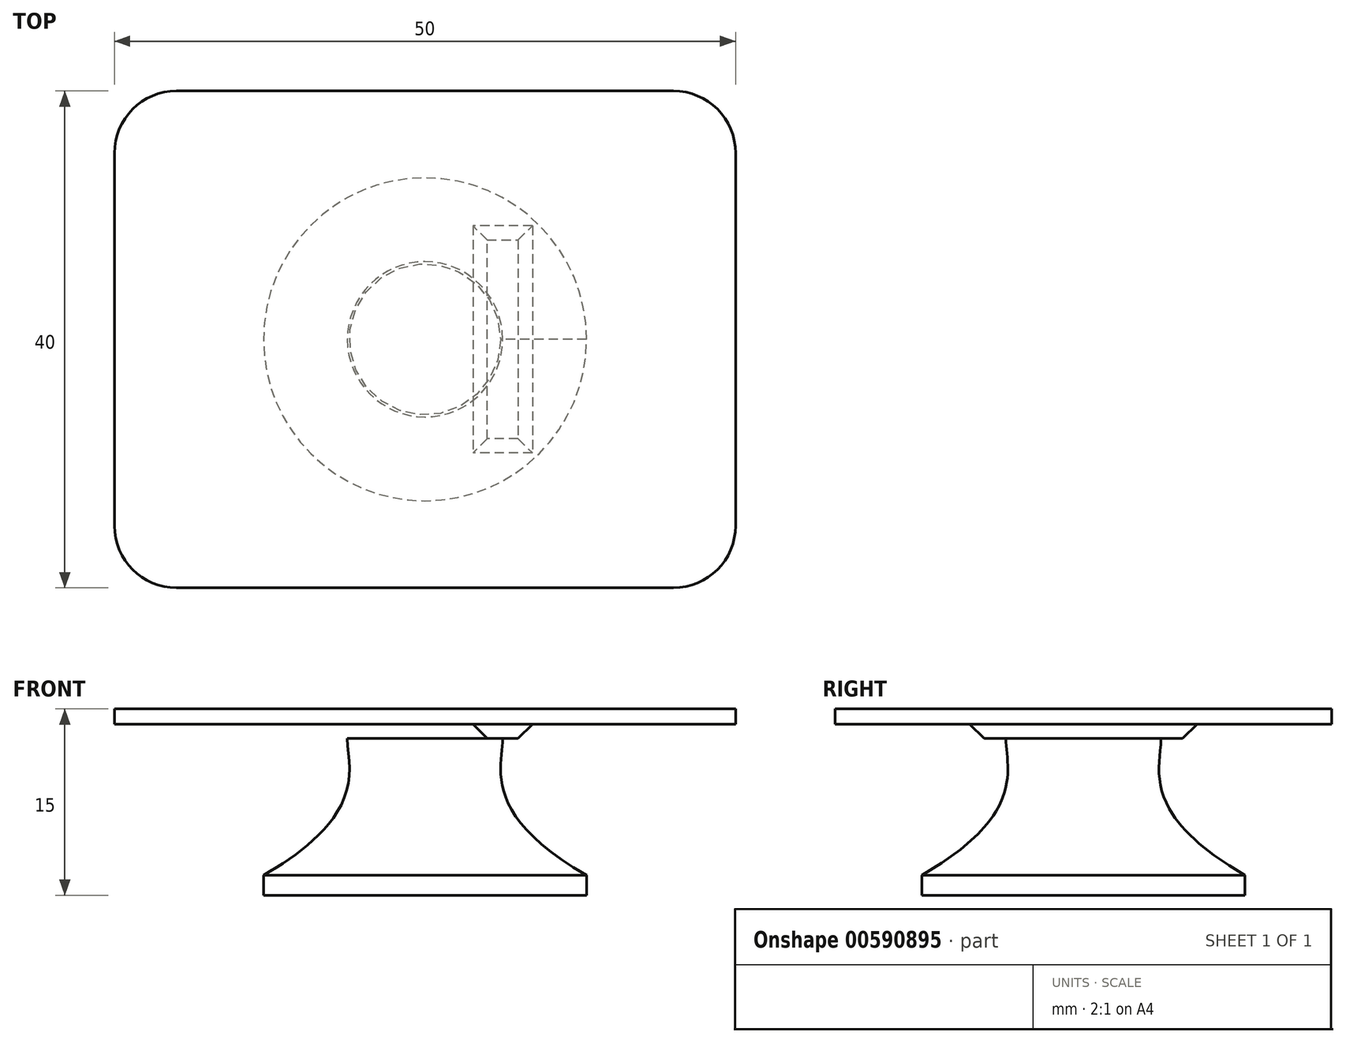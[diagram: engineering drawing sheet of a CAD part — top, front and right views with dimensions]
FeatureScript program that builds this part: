
annotation { "Feature Type Name" : "Feature", "Feature Type Description" : "" }
export const myFeature = defineFeature(function(context is Context, id is Id, definition is map)
    precondition{}
    {
        {
            var Q0;
            Q0=qCreatedBy(makeId("Front.planeOp"),FACE);
            var sketch = newSketch(context, id + "F0", { "sketchPlane" : qUnion([Q0])});
            skLineSegment(sketch, "E0.bottom", {"start": v(0, 15) * mm, "end": v(-25, 15) * mm});
            skLineSegment(sketch, "E0.top", {"start": v(0, 13.77) * mm, "end": v(-25, 13.77) * mm});
            skLineSegment(sketch, "E0.left", {"start": v(0, 15) * mm, "end": v(0, 13.77) * mm});
            skLineSegment(sketch, "E0.right", {"start": v(-25, 15) * mm, "end": v(-25, 13.77) * mm});
            skLineSegment(sketch, "E1.bottom", {"start": v(-12.5, 13.77) * mm, "end": v(0, 13.77) * mm});
            skLineSegment(sketch, "E1.top", {"start": v(-12.5, 12.62) * mm, "end": v(0, 12.62) * mm});
            skLineSegment(sketch, "E1.left", {"start": v(-12.5, 13.77) * mm, "end": v(-12.5, 12.62) * mm});
            skLineSegment(sketch, "E1.right", {"start": v(0, 13.77) * mm, "end": v(0, 12.62) * mm});
            skLineSegment(sketch, "E2.bottom", {"start": v(-13, 1.62) * mm, "end": v(0, 1.62) * mm});
            skLineSegment(sketch, "E2.top", {"start": v(-13, 0) * mm, "end": v(0, 0) * mm});
            skLineSegment(sketch, "E2.left", {"start": v(-13, 1.62) * mm, "end": v(-13, 0) * mm});
            skLineSegment(sketch, "E2.right", {"start": v(0, 1.62) * mm, "end": v(0, 0) * mm});
            skFitSpline(sketch, "E3", {"points": [v(-13, 1.62) * mm, v(-6.25, 12.62) * mm], "startDerivative": vector(25.82, 14.76) * mm, "endDerivative": vector(0.02, 6.66) * mm});
            skLineSegment(sketch, "E4", {"start": v(0, 15) * mm, "end": v(0, 0) * mm});
            skLineSegment(sketch, "E5.MirrorCS", {"start": v(13, 1.62) * mm, "end": v(13, 0) * mm});
            skLineSegment(sketch, "E6.MirrorCS", {"start": v(25, 15) * mm, "end": v(25, 13.77) * mm});
            skLineSegment(sketch, "E7.MirrorCS", {"start": v(12.5, 13.77) * mm, "end": v(12.5, 12.62) * mm});
            skFitSpline(sketch, "E8.MirrorCS", {"points": [v(13, 1.62) * mm, v(6.25, 12.62) * mm], "startDerivative": vector(-25.82, 14.76) * mm, "endDerivative": vector(-0.02, 6.66) * mm});
            skLineSegment(sketch, "E9.MirrorCS", {"start": v(13, 1.62) * mm, "end": v(0, 1.62) * mm});
            skLineSegment(sketch, "E10.MirrorCS", {"start": v(13, 0) * mm, "end": v(0, 0) * mm});
            skLineSegment(sketch, "E11.MirrorCS", {"start": v(0, 15) * mm, "end": v(25, 15) * mm});
            skLineSegment(sketch, "E12.MirrorCS", {"start": v(0, 13.77) * mm, "end": v(25, 13.77) * mm});
            skLineSegment(sketch, "E13.MirrorCS", {"start": v(12.5, 12.62) * mm, "end": v(0, 12.62) * mm});
            skLineSegment(sketch, "E14.MirrorCS", {"start": v(12.5, 13.77) * mm, "end": v(0, 13.77) * mm});
            skSolve(sketch);
        }
        {
            var Q0;
            Q0=makeQuery(id+"F0.imprint","IMPRINT",FACE,{"disambiguationData":[TD([[makeQuery(id+"F0.imprint","IMPRINT",EDGE,{"derivedFrom":sQuery(id+"F0.wireOp",EDGE,"E0.bottom")}),1.0]])]});
            var Q1;
            Q1=makeQuery(id+"F0.imprint","IMPRINT",FACE,{"disambiguationData":[TD([[makeQuery(id+"F0.imprint","IMPRINT",EDGE,{"derivedFrom":sQuery(id+"F0.wireOp",EDGE,"E0.left")}),1.0]])]});
            extrude(context, id + "F1", {"entities" : qUnion([Q0, Q1]), "endBound" : BoundingType.SYMMETRIC, "depth" : 40 * mm, "offsetDistance" : 25 * mm});
        }
        {
            var Q0;
            Q0=makeQuery(id+"F0.imprint","IMPRINT",FACE,{"disambiguationData":[TD([[makeQuery(id+"F0.imprint","IMPRINT",EDGE,{"derivedFrom":sQuery(id+"F0.wireOp",EDGE,"E1.bottom")}),-1.0]])]});
            var Q1;
            {var subQ3=sQuery(id+"F0.wireOp",EDGE,"E7.MirrorCS");Q1=makeQuery(id+"F0.imprint","IMPRINT",FACE,{"disambiguationData":[TD([[makeQuery(id+"F0.imprint","IMPRINT",EDGE,{"derivedFrom":subQ3}),-1.0]])]});}
            var Q2;
            Q2=makeQuery(id+"F0.imprint","IMPRINT",FACE,{"disambiguationData":[TD([[makeQuery(id+"F0.imprint","IMPRINT",EDGE,{"derivedFrom":sQuery(id+"F0.wireOp",EDGE,"E2.bottom")}),-1.0]])]});
            var Q3;
            Q3=makeQuery(id+"F0.imprint","IMPRINT",FACE,{"disambiguationData":[TD([[makeQuery(id+"F0.imprint","IMPRINT",EDGE,{"derivedFrom":sQuery(id+"F0.wireOp",EDGE,"E5.MirrorCS")}),-1.0]])]});
            extrude(context, id + "F2", {"entities" : qUnion([Q0, Q1, Q2, Q3]), "operationType" : NewBodyOperationType.ADD, "endBound" : BoundingType.SYMMETRIC, "depth" : 26 * mm, "offsetDistance" : 25 * mm});
        }
        {
            var Q0;
            Q0=makeQuery(id+"F0.imprint","IMPRINT",FACE,{"disambiguationData":[TD([[makeQuery(id+"F0.imprint","IMPRINT",EDGE,{"derivedFrom":sQuery(id+"F0.wireOp",EDGE,"E2.bottom")}),1.0]])]});
            var Q1;
            Q1=sQuery(id+"F0.wireOp",EDGE,"E4");
            revolve(context, id + "F3", {"entities" : qUnion([Q0]), "axis" : qUnion([Q1]), "revolveType" : RevolveType.FULL});
        }
        {
            var Q0;
            Q0=makeQuery(id+"F2.opExtrude","CAP_EDGE",EDGE,{"disambiguationData":[OSD([sQuery(id+"F0.wireOp",EDGE,"E1.top"),sQuery(id+"F0.wireOp",EDGE,"E13.MirrorCS")])],"isStart":true});
            var Q1;
            Q1=makeQuery(id+"F2.opExtrude","SWEPT_EDGE",EDGE,{"disambiguationData":[OSD([sQuery(id+"F0.wireOp",EDGE,"E1.top"),sQuery(id+"F0.wireOp",EDGE,"E1.left")])]});
            var Q2;
            Q2=makeQuery(id+"F2.opExtrude","SWEPT_EDGE",EDGE,{"disambiguationData":[OSD([sQuery(id+"F0.wireOp",EDGE,"E7.MirrorCS"),sQuery(id+"F0.wireOp",EDGE,"E13.MirrorCS")])]});
            var Q3;
            Q3=makeQuery(id+"F2.opExtrude","CAP_EDGE",EDGE,{"disambiguationData":[OSD([sQuery(id+"F0.wireOp",EDGE,"E1.top"),sQuery(id+"F0.wireOp",EDGE,"E13.MirrorCS")])],"isStart":false});
            chamfer(context, id + "F4", {"entities" : qUnion([Q0, Q1, Q2, Q3]), "width" : 5 * mm, "tangentPropagation" : true});
        }
        {
            var Q0;
            Q0=makeQuery(id+"F2.opExtrude","CAP_EDGE",EDGE,{"disambiguationData":[OSD([sQuery(id+"F0.wireOp",EDGE,"E2.left")])],"isStart":true});
            var Q1;
            Q1=makeQuery(id+"F2.opExtrude","CAP_EDGE",EDGE,{"disambiguationData":[OSD([sQuery(id+"F0.wireOp",EDGE,"E2.left")])],"isStart":false});
            var Q2;
            Q2=makeQuery(id+"F2.opExtrude","CAP_EDGE",EDGE,{"disambiguationData":[OSD([sQuery(id+"F0.wireOp",EDGE,"E5.MirrorCS")])],"isStart":false});
            var Q3;
            Q3=makeQuery(id+"F2.opExtrude","CAP_EDGE",EDGE,{"disambiguationData":[OSD([sQuery(id+"F0.wireOp",EDGE,"E5.MirrorCS")])],"isStart":true});
            fillet(context, id + "F5", {"entities" : qUnion([Q0, Q1, Q2, Q3]), "radius" : 5 * mm, "tangentPropagation" : true, "allowEdgeOverflow" : false});
        }
        {
            var Q0;
            Q0=makeQuery(id+"F1.opExtrude","CAP_EDGE",EDGE,{"disambiguationData":[OSD([sQuery(id+"F0.wireOp",EDGE,"E0.right")])],"isStart":false});
            var Q1;
            Q1=makeQuery(id+"F1.opExtrude","CAP_EDGE",EDGE,{"disambiguationData":[OSD([sQuery(id+"F0.wireOp",EDGE,"E0.right")])],"isStart":true});
            var Q2;
            Q2=makeQuery(id+"F1.opExtrude","CAP_EDGE",EDGE,{"disambiguationData":[OSD([sQuery(id+"F0.wireOp",EDGE,"E6.MirrorCS")])],"isStart":false});
            var Q3;
            Q3=makeQuery(id+"F1.opExtrude","CAP_EDGE",EDGE,{"disambiguationData":[OSD([sQuery(id+"F0.wireOp",EDGE,"E6.MirrorCS")])],"isStart":true});
            fillet(context, id + "F6", {"entities" : qUnion([Q0, Q1, Q2, Q3]), "radius" : 5 * mm, "tangentPropagation" : true, "allowEdgeOverflow" : false});
        }
        {
            var Q0;
            Q0=makeQuery(id+"F2.opExtrude","SWEPT_BODY",BODY,{"disambiguationData":[OSD([sQuery(id+"F0.wireOp",EDGE,"E2.bottom"),sQuery(id+"F0.wireOp",EDGE,"E2.top"),sQuery(id+"F0.wireOp",EDGE,"E2.left"),sQuery(id+"F0.wireOp",EDGE,"E5.MirrorCS"),sQuery(id+"F0.wireOp",EDGE,"E9.MirrorCS"),sQuery(id+"F0.wireOp",EDGE,"E10.MirrorCS")])]});
            deleteBodies(context, id + "F7", {"entities" : qUnion([Q0])});
        }
        {
            var Q0;
            Q0=makeQuery(id+"F0.imprint","IMPRINT",FACE,{"disambiguationData":[TD([[makeQuery(id+"F0.imprint","IMPRINT",EDGE,{"derivedFrom":sQuery(id+"F0.wireOp",EDGE,"E2.bottom")}),-1.0]])]});
            var Q1;
            Q1=sQuery(id+"F0.wireOp",EDGE,"E2.right");
            revolve(context, id + "F8", {"operationType" : NewBodyOperationType.ADD, "entities" : qUnion([Q0]), "axis" : qUnion([Q1]), "revolveType" : RevolveType.FULL});
        }
    });
